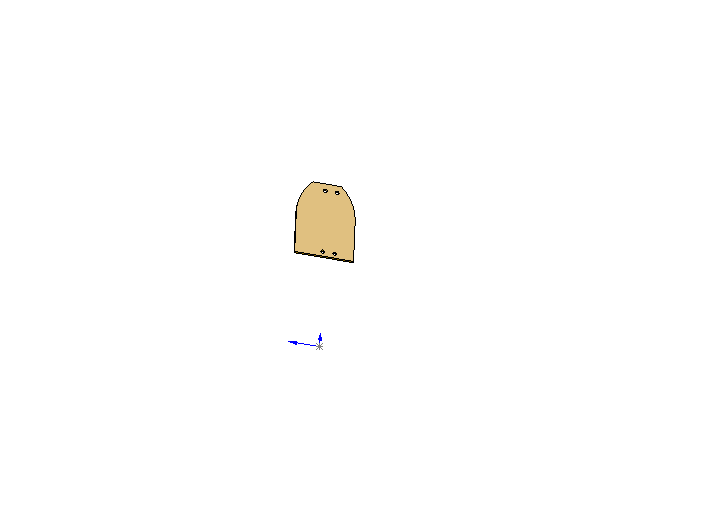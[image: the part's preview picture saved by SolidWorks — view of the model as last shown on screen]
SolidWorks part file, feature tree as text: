
SOLIDWORKS PART (.sldprt)
format: sldprt  version: not decoded by parser v0  size: 203,264 bytes
history: native  units: mm
features: sketch x4, material x1, extrude x1, hole x1, cut_extrude x1 (+12 scaffold rows collapsed)
feature tree (20):
  scaffold x12  (default folders/planes/origin — collapsed)
  material  "Material <not specified>"
  sketch  "Sketch1"  dims[c1.D1=63.5mm c1.D2=196.85mm c2.D1=9.525mm c2.D2=9.525mm c3.D1=25.4mm c3.D2=25.4mm c3.D3=~3.174041mm c3.D4=9.525mm]
  extrude  "Extrude1"  Depth=4.7625mm
  hole  "5/16 Clearance Hole1"  Diameter=8.4328mm Depth=4.7625mm
  sketch  "Sketch3"
  sketch  "Sketch2"  dims[hole-wizard template sketch: 59 standard entries collapsed; hole parameters kept: c18.Thru Hole Dia.=8.4328mm c18.Thru Hole Depth=4.7625mm]
  sketch  "Sketch5"  dims[D1=9.525mm]
  cut_extrude  "Cut-Extrude2"  [1 undecoded]
decode coverage: 5 of 7 modeling features carry decoded parameters
note: ~ marks probable driven/reference dimensions
note: 1 parameter value undecoded
note: suppression state not decoded; provenance and decode notes live in map.json
